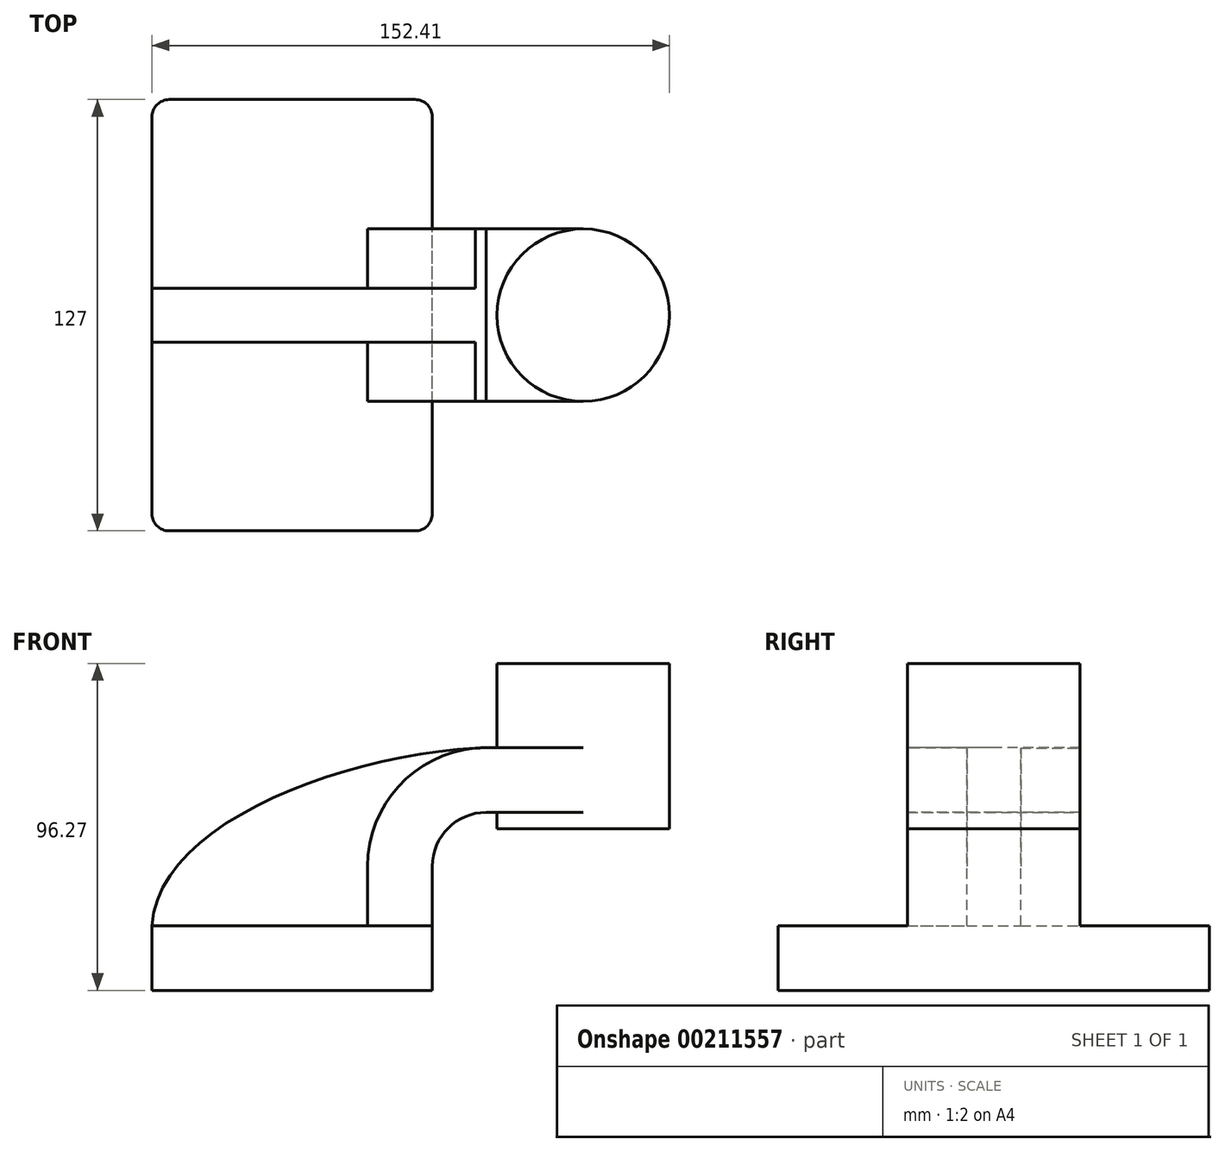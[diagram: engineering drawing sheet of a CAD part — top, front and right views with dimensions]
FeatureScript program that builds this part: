
annotation { "Feature Type Name" : "Feature", "Feature Type Description" : "" }
export const myFeature = defineFeature(function(context is Context, id is Id, definition is map)
    precondition{}
    {
        {
            var Q0;
            Q0=qCreatedBy(makeId("Front.planeOp"),FACE);
            var sketch = newSketch(context, id + "F0", { "sketchPlane" : qUnion([Q0])});
            skLineSegment(sketch, "E0.rect.bottom", {"start": v(-41.28, 9.52) * mm, "end": v(41.28, 9.52) * mm});
            skLineSegment(sketch, "E0.rect.top", {"start": v(-41.28, -9.52) * mm, "end": v(41.28, -9.52) * mm});
            skLineSegment(sketch, "E0.rect.left", {"start": v(-41.28, 9.52) * mm, "end": v(-41.28, -9.52) * mm});
            skLineSegment(sketch, "E0.rect.right", {"start": v(41.28, 9.52) * mm, "end": v(41.28, -9.52) * mm});
            skPoint(sketch, "E0.rect.middle", {"position": v(0, 0) * mm});
            skLineSegment(sketch, "E1", {"start": v(41.28, 9.52) * mm, "end": v(41.28, 27) * mm});
            skArc(sketch, "E2", {"start": v(41.28, 27) * mm, "mid": v(45.92, 38.23) * mm, "end": v(57.15, 42.88) * mm});
            skLineSegment(sketch, "E3", {"start": v(57.15, 42.88) * mm, "end": v(85.72, 42.88) * mm});
            skLineSegment(sketch, "E4.rect.bottom", {"start": v(60.32, 38.1) * mm, "end": v(111.12, 38.1) * mm});
            skLineSegment(sketch, "E4.rect.top", {"start": v(60.32, 66.68) * mm, "end": v(111.12, 66.68) * mm});
            skLineSegment(sketch, "E4.rect.left", {"start": v(60.32, 38.1) * mm, "end": v(60.32, 66.68) * mm});
            skLineSegment(sketch, "E4.rect.right", {"start": v(111.13, 38.1) * mm, "end": v(111.12, 66.68) * mm});
            skPoint(sketch, "E4.rect.middle", {"position": v(85.72, 52.39) * mm});
            skLineSegment(sketch, "E5.0", {"start": v(57.15, 61.93) * mm, "end": v(85.72, 61.93) * mm});
            skArc(sketch, "E5.1", {"start": v(22.23, 27) * mm, "mid": v(32.45, 51.7) * mm, "end": v(57.15, 61.93) * mm});
            skLineSegment(sketch, "E5.2", {"start": v(22.23, 9.52) * mm, "end": v(22.23, 27) * mm});
            skLineSegment(sketch, "E6", {"start": v(85.72, 38.1) * mm, "end": v(85.72, 66.68) * mm});
            skFitSpline(sketch, "E7", {"points": [v(-41.28, 9.53) * mm, v(57.15, 61.93) * mm], "startDerivative": vector(5.2, 92.34) * mm, "endDerivative": vector(120.92, 4.22) * mm});
            skSolve(sketch);
        }
        {
            var Q0;
            Q0=makeQuery(id+"F0.imprint","IMPRINT",FACE,{"disambiguationData":[TD([[makeQuery(id+"F0.imprint","IMPRINT",EDGE,{"derivedFrom":sQuery(id+"F0.wireOp",EDGE,"E0.rect.top")}),1.0]])]});
            extrude(context, id + "F1", {"entities" : qUnion([Q0]), "endBound" : BoundingType.SYMMETRIC, "depth" : 127 * mm});
        }
        {
            var Q0;
            {var subQ9=sQuery(id+"F0.wireOp",EDGE,"E1");Q0=makeQuery(id+"F0.imprint","IMPRINT",FACE,{"disambiguationData":[TD([[makeQuery(id+"F0.imprint","IMPRINT",EDGE,{"derivedFrom":subQ9}),1.0]])]});}
            var Q1;
            {var subQ0=sQuery(id+"F0.wireOp",EDGE,"E6");var subQ1=sQuery(id+"F0.wireOp",EDGE,"E3");var subQ2=makeQuery(id+"F0.imprint","INTERSECT",VERTEX,{"derivedFrom":[subQ1,subQ0]});Q1=makeQuery(id+"F0.imprint","IMPRINT",FACE,{"disambiguationData":[TD([[makeQuery(id+"F0.imprint","IMPRINT",EDGE,{"disambiguationData":[TD([[subQ2,1.0]])],"derivedFrom":subQ1}),1.0]])]});}
            extrude(context, id + "F2", {"entities" : qUnion([Q0, Q1]), "operationType" : NewBodyOperationType.ADD, "endBound" : BoundingType.SYMMETRIC, "depth" : 50.8 * mm});
        }
        {
            var Q0;
            {var subQ3=sQuery(id+"F0.wireOp",EDGE,"E5.2");Q0=makeQuery(id+"F0.imprint","IMPRINT",FACE,{"disambiguationData":[TD([[makeQuery(id+"F0.imprint","IMPRINT",EDGE,{"derivedFrom":subQ3}),1.0]])]});}
            extrude(context, id + "F3", {"entities" : qUnion([Q0]), "operationType" : NewBodyOperationType.ADD, "endBound" : BoundingType.SYMMETRIC, "depth" : 15.88 * mm});
        }
        {
            var Q0;
            {var subQ5=sQuery(id+"F0.wireOp",EDGE,"E4.rect.right");Q0=makeQuery(id+"F0.imprint","IMPRINT",FACE,{"disambiguationData":[TD([[makeQuery(id+"F0.imprint","IMPRINT",EDGE,{"derivedFrom":subQ5}),1.0]])]});}
            var Q1;
            Q1=sQuery(id+"F0.wireOp",EDGE,"E6");
            revolve(context, id + "F4", {"operationType" : NewBodyOperationType.ADD, "entities" : qUnion([Q0]), "axis" : qUnion([Q1]), "revolveType" : RevolveType.FULL});
        }
        {
            var Q0;
            Q0=makeQuery(id+"F1.opExtrude","CAP_EDGE",EDGE,{"disambiguationData":[OSD([sQuery(id+"F0.wireOp",EDGE,"E0.rect.right")])],"isStart":false});
            var Q1;
            Q1=makeQuery(id+"F1.opExtrude","CAP_EDGE",EDGE,{"disambiguationData":[OSD([sQuery(id+"F0.wireOp",EDGE,"E0.rect.left")])],"isStart":false});
            var Q2;
            Q2=makeQuery(id+"F1.opExtrude","CAP_EDGE",EDGE,{"disambiguationData":[OSD([sQuery(id+"F0.wireOp",EDGE,"E0.rect.right")])],"isStart":true});
            var Q3;
            Q3=makeQuery(id+"F1.opExtrude","CAP_EDGE",EDGE,{"disambiguationData":[OSD([sQuery(id+"F0.wireOp",EDGE,"E0.rect.left")])],"isStart":true});
            fillet(context, id + "F5", {"entities" : qUnion([Q0, Q1, Q2, Q3]), "radius" : 5.08 * mm, "tangentPropagation" : true, "allowEdgeOverflow" : false});
        }
        {
            var Q0;
            {var subQ4=sQuery(id+"F0.wireOp",EDGE,"E0.rect.bottom");var subQ5=sQuery(id+"F0.wireOp",EDGE,"E0.rect.right");var subQ6=sQuery(id+"F0.wireOp",EDGE,"E0.rect.left");Q0=makeQuery(id+"F3.boolean.opBoolean","SPLIT",FACE,{"disambiguationData":[TD([makeQuery(id+"F1.opExtrude","CAP_FACE",FACE,{"disambiguationData":[OSD([subQ4,sQuery(id+"F0.wireOp",EDGE,"E0.rect.top"),subQ6,subQ5])],"isStart":false})])],"derivedFrom":makeQuery(id+"F1.opExtrude","SWEPT_FACE",FACE,{"disambiguationData":[OSD([subQ4])]})});}
            extrude(context, id + "F6", {"entities" : qUnion([Q0]), "operationType" : NewBodyOperationType.ADD, "oppositeDirection" : true, "depth" : 6.1 * mm});
        }
        {
            var Q0;
            Q0=makeQuery(id+"F4.opRevolve","SWEPT_FACE",FACE,{"disambiguationData":[OSD([sQuery(id+"F0.wireOp",EDGE,"E4.rect.top")])]});
            extrude(context, id + "F7", {"entities" : qUnion([Q0]), "operationType" : NewBodyOperationType.ADD, "depth" : 20.07 * mm});
        }
    });
